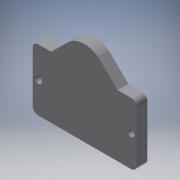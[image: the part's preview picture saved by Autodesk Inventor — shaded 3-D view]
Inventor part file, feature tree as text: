
AUTODESK INVENTOR PART (.ipt)
format: ipt  version: 2016 (Build 200138000, 138)  size: 166,400 bytes
history: native  units: mm (DEFAULTED — no unit token found)
features: other x11, extrude x3, hole x2, sketch x2
ambient origin geometry x8: Origin, YZ Plane, XZ Plane, XY Plane, X Axis, Y Axis, Z Axis, Center Point
bodies: Solid1 (feature_tree)
feature tree (18):
  other  "Blocks"
  extrude  "Extrusion1"  Depth=0.762mm
  extrude  "Extrusion8"  Depth=1.524mm TaperAngle=0.0deg
  extrude  "Extrusion9"  Depth=0.762mm
  hole  "Hole9"  [1 undecoded]
  hole  "Hole10"  [1 undecoded]
  other  "Block1"
  other  "Block2"
  other  "Block3"
  other  "Block4"
  sketch  "Sketch13"  dims[d2=1.524mm d3=0.0mm d110=0.762mm]
  other  "Block5"
  other  "Block6"
  sketch  "Sketch16"  dims[d111=0.762mm d132=1.524mm d133=0.0mm d153=0.762mm d216=25.4mm d217=25.4mm d157=1.016mm d158=2.3876mm d159=9.525mm d160=6.35mm d161=14.3117mm d162=1.524mm d163=0.0mm d218=25.4mm d219=25.4mm d166=1.016mm d167=2.3876mm d168=9.525mm d169=6.35mm d170=14.3117mm d171=1.524mm d172=0.0mm d177=0.762mm d178=0.762mm d179=0.762mm d180=0.762mm d181=1.524mm d182=0.0mm d22=25.4mm d23=25.4mm d63=25.4mm d64=25.4mm d81=25.4mm d82=25.4mm d108=25.4mm d109=25.4mm d155=25.4mm d156=25.4mm]
  other  "Block1:2"
  other  "Block2:2"
  other  "Block3:2"
  other  "Block6:1"
note: 2 required parameter values undecoded (feature->parameter linkage not recoverable at this tier; creation-order binding heuristic only, values carry confidence <= 0.55)
